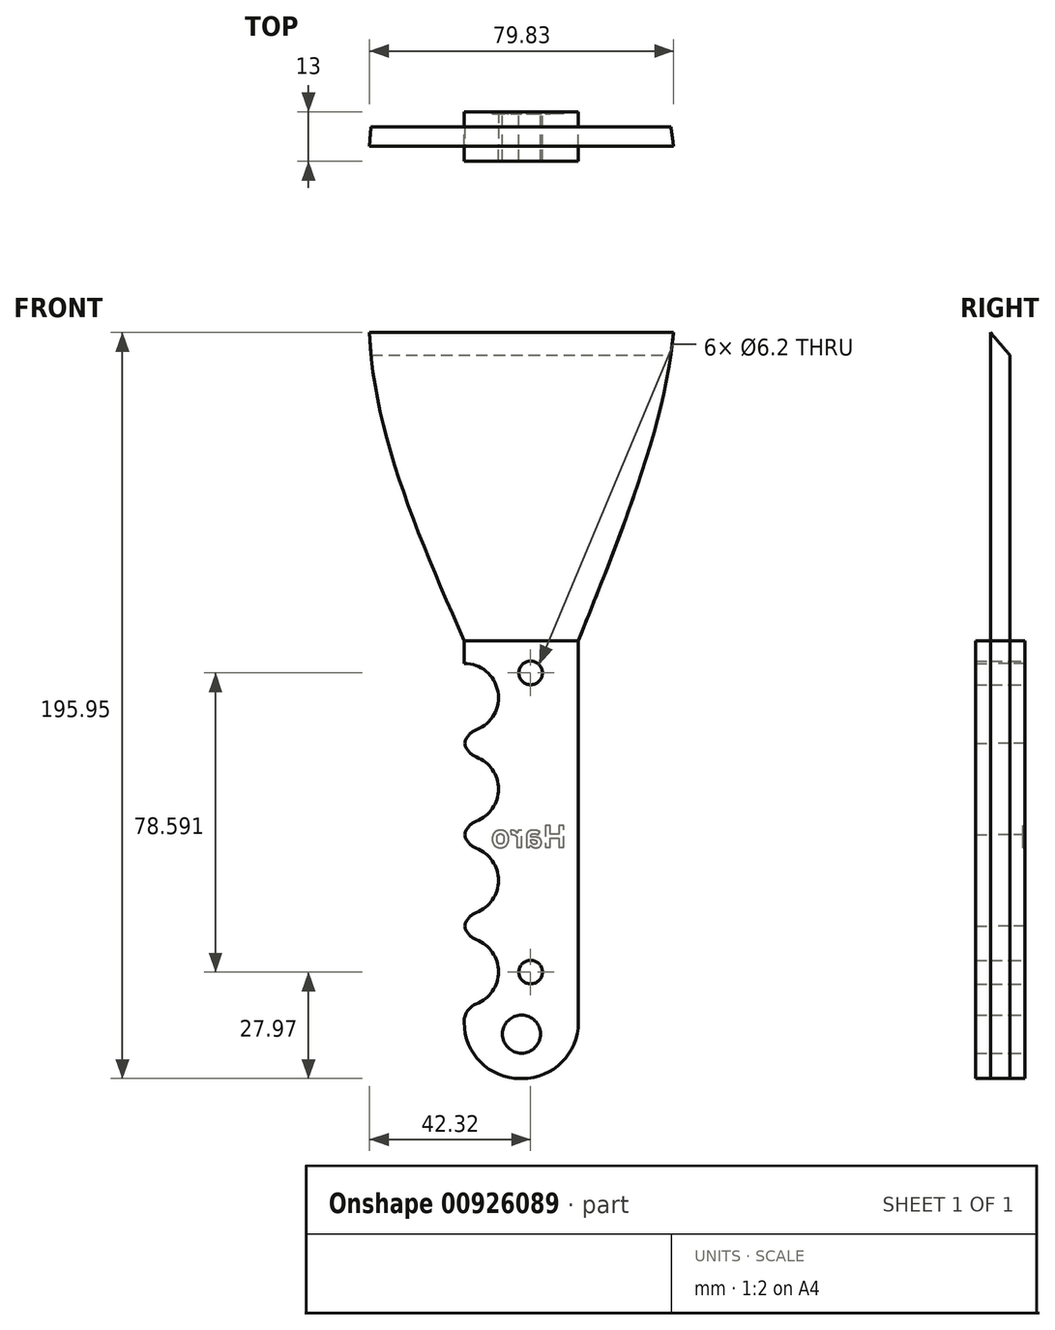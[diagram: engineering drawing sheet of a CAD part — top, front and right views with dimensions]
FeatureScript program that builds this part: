
annotation { "Feature Type Name" : "Feature", "Feature Type Description" : "" }
export const myFeature = defineFeature(function(context is Context, id is Id, definition is map)
    precondition{}
    {
        {
            var Q0;
            Q0=qCreatedBy(makeId("Front.planeOp"),FACE);
            var sketch = newSketch(context, id + "F0", { "sketchPlane" : qUnion([Q0])});
            skLineSegment(sketch, "E0.bottom", {"start": v(-42.47, 148.7) * mm, "end": v(37.53, 148.7) * mm});
            skLineSegment(sketch, "E0.top", {"start": v(-42.47, -51.3) * mm, "end": v(37.53, -51.3) * mm});
            skLineSegment(sketch, "E0.left", {"start": v(-42.47, 148.7) * mm, "end": v(-42.47, -51.3) * mm});
            skLineSegment(sketch, "E0.right", {"start": v(37.53, 148.7) * mm, "end": v(37.53, -51.3) * mm});
            skSolve(sketch);
        }
        {
            var Q0;
            Q0=makeQuery(id+"F0.imprint","IMPRINT",FACE,{"disambiguationData":[TD([[makeQuery(id+"F0.imprint","IMPRINT",EDGE,{"derivedFrom":sQuery(id+"F0.wireOp",EDGE,"E0.bottom")}),-1.0]])]});
            var sketch = newSketch(context, id + "F1", { "sketchPlane" : qUnion([Q0])});
            skLineSegment(sketch, "E1.0", {"start": v(-42.47, 63.7) * mm, "end": v(37.53, 63.7) * mm});
            skLineSegment(sketch, "E2.0", {"start": v(-17.47, 148.7) * mm, "end": v(-17.47, -51.3) * mm});
            skLineSegment(sketch, "E3.0", {"start": v(12.53, 148.7) * mm, "end": v(12.53, -51.3) * mm});
            skFitSpline(sketch, "E4", {"points": [v(-17.47, 63.7) * mm, v(-42.38, 149.23) * mm, v(-17.47, 227.04) * mm], "startDerivative": vector(-74.22, 169.58) * mm, "endDerivative": vector(75.3, 157.02) * mm});
            skFitSpline(sketch, "E5", {"points": [v(12.53, 63.7) * mm, v(37.76, 148.7) * mm, v(27.55, 195.49) * mm], "startDerivative": vector(63.33, 158.14) * mm, "endDerivative": vector(-38.49, 102.62) * mm});
            skSolve(sketch);
        }
        {
            var Q0;
            {var subQ0=sQuery(id+"F1.wireOp",EDGE,"E2.0");var subQ5=makeQuery(id+"F0.imprint","IMPRINT",EDGE,{"derivedFrom":sQuery(id+"F0.wireOp",EDGE,"E0.bottom")});var subQ6=makeQuery(id+"F1.imprint","INTERSECT",VERTEX,{"derivedFrom":[subQ5,subQ0]});Q0=makeQuery(id+"F1.imprint","IMPRINT",FACE,{"disambiguationData":[TD([[makeQuery(id+"F1.imprint","IMPRINT",EDGE,{"disambiguationData":[TD([[subQ6,-1.0]])],"derivedFrom":subQ5}),-1.0]])]});}
            var Q1;
            {var subQ0=sQuery(id+"F1.wireOp",EDGE,"E2.0");var subQ1=makeQuery(id+"F0.imprint","IMPRINT",EDGE,{"derivedFrom":sQuery(id+"F0.wireOp",EDGE,"E0.bottom")});var subQ2=makeQuery(id+"F1.imprint","INTERSECT",VERTEX,{"derivedFrom":[subQ1,subQ0]});Q1=makeQuery(id+"F1.imprint","IMPRINT",FACE,{"disambiguationData":[TD([[makeQuery(id+"F1.imprint","IMPRINT",EDGE,{"disambiguationData":[TD([[subQ2,1.0]])],"derivedFrom":subQ1}),-1.0]])]});}
            var Q2;
            {var subQ1=makeQuery(id+"F0.imprint","IMPRINT",EDGE,{"derivedFrom":sQuery(id+"F0.wireOp",EDGE,"E0.bottom")});var subQ5=makeQuery(id+"F0.imprint","IMPRINT",EDGE,{"derivedFrom":sQuery(id+"F0.wireOp",EDGE,"E0.right")});var subQ7=makeQuery(id+"F1.imprint","INTERSECT",VERTEX,{"derivedFrom":[subQ1,subQ5]});Q2=makeQuery(id+"F1.imprint","IMPRINT",FACE,{"disambiguationData":[TD([[makeQuery(id+"F1.imprint","IMPRINT",EDGE,{"disambiguationData":[TD([[subQ7,1.0]])],"derivedFrom":subQ1}),-1.0]])]});}
            var Q3;
            {var subQ0=sQuery(id+"F1.wireOp",EDGE,"E2.0");var subQ5=makeQuery(id+"F0.imprint","IMPRINT",EDGE,{"derivedFrom":sQuery(id+"F0.wireOp",EDGE,"E0.top")});var subQ7=makeQuery(id+"F1.imprint","INTERSECT",VERTEX,{"derivedFrom":[subQ5,subQ0]});Q3=makeQuery(id+"F1.imprint","IMPRINT",FACE,{"disambiguationData":[TD([[makeQuery(id+"F1.imprint","IMPRINT",EDGE,{"disambiguationData":[TD([[subQ7,-1.0]])],"derivedFrom":subQ5}),1.0]])]});}
            extrude(context, id + "F2", {"entities" : qUnion([Q0, Q1, Q2, Q3]), "depth" : 5 * mm, "offsetDistance" : 25 * mm});
        }
        {
            var Q0;
            Q0=makeQuery(id+"F2.opExtrude","CAP_FACE",FACE,{"disambiguationData":[OSD([sQuery(id+"F0.wireOp",EDGE,"E0.bottom"),sQuery(id+"F0.wireOp",EDGE,"E0.top"),sQuery(id+"F0.wireOp",EDGE,"E0.right"),sQuery(id+"F1.wireOp",EDGE,"E2.0"),sQuery(id+"F1.wireOp",EDGE,"E3.0"),sQuery(id+"F1.wireOp",EDGE,"E4"),sQuery(id+"F1.wireOp",EDGE,"E5")])],"isStart":false});
            var sketch = newSketch(context, id + "F3", { "sketchPlane" : qUnion([Q0])});
            skCircle(sketch, "E6", {"center": v(-17.47, 48.75) * mm, "radius": 9 * mm});
            skCircle(sketch, "E7", {"center": v(-17.47, 24.75) * mm, "radius": 9 * mm});
            skCircle(sketch, "E8", {"center": v(-17.47, 0.75) * mm, "radius": 9 * mm});
            skCircle(sketch, "E9", {"center": v(-17.47, -23.25) * mm, "radius": 9 * mm});
            skCircle(sketch, "E10", {"center": v(18.56, 49.84) * mm, "radius": 9 * mm});
            skSolve(sketch);
        }
        {
            var Q0;
            {var subQ0=sQuery(id+"F3.wireOp",EDGE,"E6");var subQ1=makeQuery(id+"F2.opExtrude","CAP_EDGE",EDGE,{"disambiguationData":[OSD([sQuery(id+"F1.wireOp",EDGE,"E2.0")])],"isStart":false});var subQ2=makeQuery(id+"F3.imprint","INTERSECT",VERTEX,{"disambiguationData":[OD(0.0)],"derivedFrom":[subQ1,subQ0]});Q0=makeQuery(id+"F3.imprint","IMPRINT",FACE,{"disambiguationData":[TD([[makeQuery(id+"F3.imprint","IMPRINT",EDGE,{"disambiguationData":[TD([[subQ2,1.0]])],"derivedFrom":subQ0}),1.0]])]});}
            var Q1;
            {var subQ0=sQuery(id+"F3.wireOp",EDGE,"E7");var subQ1=makeQuery(id+"F2.opExtrude","CAP_EDGE",EDGE,{"disambiguationData":[OSD([sQuery(id+"F1.wireOp",EDGE,"E2.0")])],"isStart":false});var subQ2=makeQuery(id+"F3.imprint","INTERSECT",VERTEX,{"disambiguationData":[OD(0.0)],"derivedFrom":[subQ1,subQ0]});Q1=makeQuery(id+"F3.imprint","IMPRINT",FACE,{"disambiguationData":[TD([[makeQuery(id+"F3.imprint","IMPRINT",EDGE,{"disambiguationData":[TD([[subQ2,1.0]])],"derivedFrom":subQ0}),1.0]])]});}
            var Q2;
            {var subQ0=sQuery(id+"F3.wireOp",EDGE,"E8");var subQ1=makeQuery(id+"F2.opExtrude","CAP_EDGE",EDGE,{"disambiguationData":[OSD([sQuery(id+"F1.wireOp",EDGE,"E2.0")])],"isStart":false});var subQ2=makeQuery(id+"F3.imprint","INTERSECT",VERTEX,{"disambiguationData":[OD(0.0)],"derivedFrom":[subQ1,subQ0]});Q2=makeQuery(id+"F3.imprint","IMPRINT",FACE,{"disambiguationData":[TD([[makeQuery(id+"F3.imprint","IMPRINT",EDGE,{"disambiguationData":[TD([[subQ2,-1.0]])],"derivedFrom":subQ0}),1.0]])]});}
            var Q3;
            {var subQ0=sQuery(id+"F3.wireOp",EDGE,"E9");var subQ1=makeQuery(id+"F2.opExtrude","CAP_EDGE",EDGE,{"disambiguationData":[OSD([sQuery(id+"F1.wireOp",EDGE,"E2.0")])],"isStart":false});var subQ2=makeQuery(id+"F3.imprint","INTERSECT",VERTEX,{"disambiguationData":[OD(0.0)],"derivedFrom":[subQ1,subQ0]});Q3=makeQuery(id+"F3.imprint","IMPRINT",FACE,{"disambiguationData":[TD([[makeQuery(id+"F3.imprint","IMPRINT",EDGE,{"disambiguationData":[TD([[subQ2,-1.0]])],"derivedFrom":subQ0}),1.0]])]});}
            var Q4;
            {var subQ0=sQuery(id+"F3.wireOp",EDGE,"E10");var subQ1=makeQuery(id+"F2.opExtrude","CAP_EDGE",EDGE,{"disambiguationData":[OSD([sQuery(id+"F1.wireOp",EDGE,"E3.0")])],"isStart":false});var subQ2=makeQuery(id+"F3.imprint","INTERSECT",VERTEX,{"disambiguationData":[OD(0.0)],"derivedFrom":[subQ1,subQ0]});Q4=makeQuery(id+"F3.imprint","IMPRINT",FACE,{"disambiguationData":[TD([[makeQuery(id+"F3.imprint","IMPRINT",EDGE,{"disambiguationData":[TD([[subQ2,1.0]])],"derivedFrom":subQ0}),1.0]])]});}
            extrude(context, id + "F4", {"entities" : qUnion([Q0, Q1, Q2, Q3, Q4]), "operationType" : NewBodyOperationType.REMOVE, "oppositeDirection" : true, "depth" : 25 * mm, "offsetDistance" : 25 * mm});
        }
        {
            var Q0;
            {var subQ0=sQuery(id+"F3.wireOp",EDGE,"E9");var subQ1=sQuery(id+"F1.wireOp",EDGE,"E2.0");Q0=makeQuery(id+"F4.boolean.opBoolean","COPY",EDGE,{"derivedFrom":makeQuery(id+"F4.opExtrude","SWEPT_EDGE",EDGE,{"disambiguationData":[OSD([subQ1,subQ0]),TDD([makeQuery(id+"F3.imprint","INTERSECT",VERTEX,{"disambiguationData":[OD(1.0)],"derivedFrom":[makeQuery(id+"F2.opExtrude","CAP_EDGE",EDGE,{"disambiguationData":[OSD([subQ1])],"isStart":false}),subQ0]})])]})});}
            var Q1;
            {var subQ0=sQuery(id+"F3.wireOp",EDGE,"E8");var subQ1=sQuery(id+"F1.wireOp",EDGE,"E2.0");Q1=makeQuery(id+"F4.boolean.opBoolean","COPY",EDGE,{"derivedFrom":makeQuery(id+"F4.opExtrude","SWEPT_EDGE",EDGE,{"disambiguationData":[OSD([subQ1,subQ0]),TDD([makeQuery(id+"F3.imprint","INTERSECT",VERTEX,{"disambiguationData":[OD(0.0)],"derivedFrom":[makeQuery(id+"F2.opExtrude","CAP_EDGE",EDGE,{"disambiguationData":[OSD([subQ1])],"isStart":false}),subQ0]})])]})});}
            var Q2;
            {var subQ0=sQuery(id+"F3.wireOp",EDGE,"E8");var subQ1=sQuery(id+"F1.wireOp",EDGE,"E2.0");Q2=makeQuery(id+"F4.boolean.opBoolean","COPY",EDGE,{"derivedFrom":makeQuery(id+"F4.opExtrude","SWEPT_EDGE",EDGE,{"disambiguationData":[OSD([subQ1,subQ0]),TDD([makeQuery(id+"F3.imprint","INTERSECT",VERTEX,{"disambiguationData":[OD(1.0)],"derivedFrom":[makeQuery(id+"F2.opExtrude","CAP_EDGE",EDGE,{"disambiguationData":[OSD([subQ1])],"isStart":false}),subQ0]})])]})});}
            var Q3;
            {var subQ0=sQuery(id+"F3.wireOp",EDGE,"E7");var subQ1=sQuery(id+"F1.wireOp",EDGE,"E2.0");Q3=makeQuery(id+"F4.boolean.opBoolean","COPY",EDGE,{"derivedFrom":makeQuery(id+"F4.opExtrude","SWEPT_EDGE",EDGE,{"disambiguationData":[OSD([subQ1,subQ0]),TDD([makeQuery(id+"F3.imprint","INTERSECT",VERTEX,{"disambiguationData":[OD(1.0)],"derivedFrom":[makeQuery(id+"F2.opExtrude","CAP_EDGE",EDGE,{"disambiguationData":[OSD([subQ1])],"isStart":false}),subQ0]})])]})});}
            var Q4;
            {var subQ0=sQuery(id+"F3.wireOp",EDGE,"E7");var subQ1=sQuery(id+"F1.wireOp",EDGE,"E2.0");Q4=makeQuery(id+"F4.boolean.opBoolean","COPY",EDGE,{"derivedFrom":makeQuery(id+"F4.opExtrude","SWEPT_EDGE",EDGE,{"disambiguationData":[OSD([subQ1,subQ0]),TDD([makeQuery(id+"F3.imprint","INTERSECT",VERTEX,{"disambiguationData":[OD(0.0)],"derivedFrom":[makeQuery(id+"F2.opExtrude","CAP_EDGE",EDGE,{"disambiguationData":[OSD([subQ1])],"isStart":false}),subQ0]})])]})});}
            var Q5;
            {var subQ0=sQuery(id+"F3.wireOp",EDGE,"E6");var subQ1=sQuery(id+"F1.wireOp",EDGE,"E2.0");Q5=makeQuery(id+"F4.boolean.opBoolean","COPY",EDGE,{"derivedFrom":makeQuery(id+"F4.opExtrude","SWEPT_EDGE",EDGE,{"disambiguationData":[OSD([subQ1,subQ0]),TDD([makeQuery(id+"F3.imprint","INTERSECT",VERTEX,{"disambiguationData":[OD(1.0)],"derivedFrom":[makeQuery(id+"F2.opExtrude","CAP_EDGE",EDGE,{"disambiguationData":[OSD([subQ1])],"isStart":false}),subQ0]})])]})});}
            var Q6;
            {var subQ0=sQuery(id+"F3.wireOp",EDGE,"E6");var subQ1=sQuery(id+"F1.wireOp",EDGE,"E2.0");Q6=makeQuery(id+"F4.boolean.opBoolean","COPY",EDGE,{"derivedFrom":makeQuery(id+"F4.opExtrude","SWEPT_EDGE",EDGE,{"disambiguationData":[OSD([subQ1,subQ0]),TDD([makeQuery(id+"F3.imprint","INTERSECT",VERTEX,{"disambiguationData":[OD(0.0)],"derivedFrom":[makeQuery(id+"F2.opExtrude","CAP_EDGE",EDGE,{"disambiguationData":[OSD([subQ1])],"isStart":false}),subQ0]})])]})});}
            var Q7;
            {var subQ0=sQuery(id+"F3.wireOp",EDGE,"E9");var subQ1=sQuery(id+"F1.wireOp",EDGE,"E2.0");Q7=makeQuery(id+"F4.boolean.opBoolean","COPY",EDGE,{"derivedFrom":makeQuery(id+"F4.opExtrude","SWEPT_EDGE",EDGE,{"disambiguationData":[OSD([subQ1,subQ0]),TDD([makeQuery(id+"F3.imprint","INTERSECT",VERTEX,{"disambiguationData":[OD(0.0)],"derivedFrom":[makeQuery(id+"F2.opExtrude","CAP_EDGE",EDGE,{"disambiguationData":[OSD([subQ1])],"isStart":false}),subQ0]})])]})});}
            var Q8;
            {var subQ0=sQuery(id+"F3.wireOp",EDGE,"E10");var subQ1=sQuery(id+"F1.wireOp",EDGE,"E3.0");Q8=makeQuery(id+"F4.boolean.opBoolean","COPY",EDGE,{"derivedFrom":makeQuery(id+"F4.opExtrude","SWEPT_EDGE",EDGE,{"disambiguationData":[OSD([subQ1,subQ0]),TDD([makeQuery(id+"F3.imprint","INTERSECT",VERTEX,{"disambiguationData":[OD(1.0)],"derivedFrom":[makeQuery(id+"F2.opExtrude","CAP_EDGE",EDGE,{"disambiguationData":[OSD([subQ1])],"isStart":false}),subQ0]})])]})});}
            var Q9;
            {var subQ0=sQuery(id+"F3.wireOp",EDGE,"E10");var subQ1=sQuery(id+"F1.wireOp",EDGE,"E3.0");Q9=makeQuery(id+"F4.boolean.opBoolean","COPY",EDGE,{"derivedFrom":makeQuery(id+"F4.opExtrude","SWEPT_EDGE",EDGE,{"disambiguationData":[OSD([subQ1,subQ0]),TDD([makeQuery(id+"F3.imprint","INTERSECT",VERTEX,{"disambiguationData":[OD(0.0)],"derivedFrom":[makeQuery(id+"F2.opExtrude","CAP_EDGE",EDGE,{"disambiguationData":[OSD([subQ1])],"isStart":false}),subQ0]})])]})});}
            fillet(context, id + "F5", {"entities" : qUnion([Q0, Q1, Q2, Q3, Q4, Q5, Q6, Q7, Q8, Q9]), "radius" : 5 * mm, "tangentPropagation" : true, "allowEdgeOverflow" : false});
        }
        {
            var Q0;
            Q0=makeQuery(id+"F2.opExtrude","SWEPT_EDGE",EDGE,{"disambiguationData":[OSD([sQuery(id+"F0.wireOp",EDGE,"E0.top"),sQuery(id+"F1.wireOp",EDGE,"E3.0")])]});
            var Q1;
            Q1=makeQuery(id+"F2.opExtrude","SWEPT_EDGE",EDGE,{"disambiguationData":[OSD([sQuery(id+"F0.wireOp",EDGE,"E0.top"),sQuery(id+"F1.wireOp",EDGE,"E2.0")])]});
            fillet(context, id + "F6", {"entities" : qUnion([Q0, Q1]), "radius" : 14.73 * mm, "tangentPropagation" : true, "allowEdgeOverflow" : false});
        }
        {
            var Q0;
            Q0=makeQuery(id+"F2.opExtrude","CAP_FACE",FACE,{"disambiguationData":[OSD([sQuery(id+"F0.wireOp",EDGE,"E0.bottom"),sQuery(id+"F0.wireOp",EDGE,"E0.top"),sQuery(id+"F0.wireOp",EDGE,"E0.right"),sQuery(id+"F1.wireOp",EDGE,"E2.0"),sQuery(id+"F1.wireOp",EDGE,"E3.0"),sQuery(id+"F1.wireOp",EDGE,"E4"),sQuery(id+"F1.wireOp",EDGE,"E5")])],"isStart":false});
            var sketch = newSketch(context, id + "F7", { "sketchPlane" : qUnion([Q0])});
            skLineSegment(sketch, "E11", {"start": v(-17.47, 63.7) * mm, "end": v(12.53, 63.7) * mm});
            skSolve(sketch);
        }
        {
            var Q0;
            Q0=makeQuery(id+"F7.imprint","IMPRINT",FACE,{"disambiguationData":[TD([[makeQuery(id+"F7.imprint","IMPRINT",EDGE,{"derivedFrom":sQuery(id+"F7.wireOp",EDGE,"E11")}),-1.0]])]});
            extrude(context, id + "F8", {"entities" : qUnion([Q0]), "depth" : 4 * mm, "offsetDistance" : 25 * mm});
        }
        {
            var Q0;
            Q0=makeQuery(id+"F2.opExtrude","CAP_FACE",FACE,{"disambiguationData":[OSD([sQuery(id+"F0.wireOp",EDGE,"E0.bottom"),sQuery(id+"F0.wireOp",EDGE,"E0.top"),sQuery(id+"F0.wireOp",EDGE,"E0.right"),sQuery(id+"F1.wireOp",EDGE,"E2.0"),sQuery(id+"F1.wireOp",EDGE,"E3.0"),sQuery(id+"F1.wireOp",EDGE,"E4"),sQuery(id+"F1.wireOp",EDGE,"E5")])],"isStart":true});
            var sketch = newSketch(context, id + "F9", { "sketchPlane" : qUnion([Q0])});
            skLineSegment(sketch, "E12", {"start": v(-12.53, 63.7) * mm, "end": v(17.47, 63.7) * mm});
            skSolve(sketch);
        }
        {
            var Q0;
            Q0=makeQuery(id+"F9.imprint","IMPRINT",FACE,{"disambiguationData":[TD([[makeQuery(id+"F9.imprint","IMPRINT",EDGE,{"derivedFrom":sQuery(id+"F9.wireOp",EDGE,"E12")}),-1.0]])]});
            extrude(context, id + "F10", {"entities" : qUnion([Q0]), "depth" : 4 * mm, "offsetDistance" : 25 * mm});
        }
        {
            var Q0;
            Q0=makeQuery(id+"F10.opExtrude","CAP_FACE",FACE,{"disambiguationData":[OSD([sQuery(id+"F0.wireOp",EDGE,"E0.bottom"),sQuery(id+"F0.wireOp",EDGE,"E0.top"),sQuery(id+"F0.wireOp",EDGE,"E0.right"),sQuery(id+"F1.wireOp",EDGE,"E2.0"),sQuery(id+"F1.wireOp",EDGE,"E3.0"),sQuery(id+"F1.wireOp",EDGE,"E4"),sQuery(id+"F1.wireOp",EDGE,"E5"),sQuery(id+"F3.wireOp",EDGE,"E6"),sQuery(id+"F3.wireOp",EDGE,"E7"),sQuery(id+"F3.wireOp",EDGE,"E8"),sQuery(id+"F3.wireOp",EDGE,"E9"),sQuery(id+"F3.wireOp",EDGE,"E10"),sQuery(id+"F9.wireOp",EDGE,"E12")])],"isStart":false});
            var sketch = newSketch(context, id + "F11", { "sketchPlane" : qUnion([Q0])});
            skCircle(sketch, "E13", {"center": v(0, 55.26) * mm, "radius": 3.1 * mm});
            skCircle(sketch, "E14", {"center": v(0, -23.33) * mm, "radius": 3.1 * mm});
            skCircle(sketch, "E15", {"center": v(2.4, -39.62) * mm, "radius": 5 * mm});
            skSolve(sketch);
        }
        {
            var Q0;
            Q0=makeQuery(id+"F11.imprint","IMPRINT",FACE,{"disambiguationData":[TD([[makeQuery(id+"F11.imprint","IMPRINT",EDGE,{"derivedFrom":sQuery(id+"F11.wireOp",EDGE,"E13")}),1.0]])]});
            var Q1;
            Q1=makeQuery(id+"F11.imprint","IMPRINT",FACE,{"disambiguationData":[TD([[makeQuery(id+"F11.imprint","IMPRINT",EDGE,{"derivedFrom":sQuery(id+"F11.wireOp",EDGE,"E14")}),1.0]])]});
            var Q2;
            Q2=makeQuery(id+"F11.imprint","IMPRINT",FACE,{"disambiguationData":[TD([[makeQuery(id+"F11.imprint","IMPRINT",EDGE,{"derivedFrom":sQuery(id+"F11.wireOp",EDGE,"E15")}),1.0]])]});
            extrude(context, id + "F12", {"entities" : qUnion([Q0, Q1, Q2]), "operationType" : NewBodyOperationType.REMOVE, "oppositeDirection" : true, "depth" : 25 * mm, "offsetDistance" : 25 * mm});
        }
        {
            var Q0;
            Q0=makeQuery(id+"F2.opExtrude","CAP_EDGE",EDGE,{"disambiguationData":[OSD([sQuery(id+"F0.wireOp",EDGE,"E0.bottom")])],"isStart":true});
            chamfer(context, id + "F13", {"entities" : qUnion([Q0]), "chamferType" : ChamferType.OFFSET_ANGLE, "width" : 10 * mm, "oppositeDirection" : false, "angle" : 40 * degree, "tangentPropagation" : true});
        }
        {
            var Q0;
            Q0=makeQuery(id+"F10.opExtrude","CAP_FACE",FACE,{"disambiguationData":[OSD([sQuery(id+"F0.wireOp",EDGE,"E0.bottom"),sQuery(id+"F0.wireOp",EDGE,"E0.top"),sQuery(id+"F0.wireOp",EDGE,"E0.right"),sQuery(id+"F1.wireOp",EDGE,"E2.0"),sQuery(id+"F1.wireOp",EDGE,"E3.0"),sQuery(id+"F1.wireOp",EDGE,"E4"),sQuery(id+"F1.wireOp",EDGE,"E5"),sQuery(id+"F3.wireOp",EDGE,"E6"),sQuery(id+"F3.wireOp",EDGE,"E7"),sQuery(id+"F3.wireOp",EDGE,"E8"),sQuery(id+"F3.wireOp",EDGE,"E9"),sQuery(id+"F3.wireOp",EDGE,"E10"),sQuery(id+"F9.wireOp",EDGE,"E12")])],"isStart":false});
            var sketch = newSketch(context, id + "F14", { "sketchPlane" : qUnion([Q0])});
            skText(sketch, "E16", { "text": "Haro\n", "fontName": "OpenSans-Bold.ttf"});
            const initialGuessF14  = {"E16": [-0.00939, 0.00942, 1, 0, 0.00585]};
            skSetInitialGuess(sketch, initialGuessF14);
            skSolve(sketch);
        }
        {
            var Q0;
            Q0 = qSketchRegion(id + "F14", true);
            extrude(context, id + "F15", {"entities" : qUnion([Q0]), "operationType" : NewBodyOperationType.REMOVE, "oppositeDirection" : true, "depth" : .5 * mm, "offsetDistance" : 25 * mm});
        }
    });
